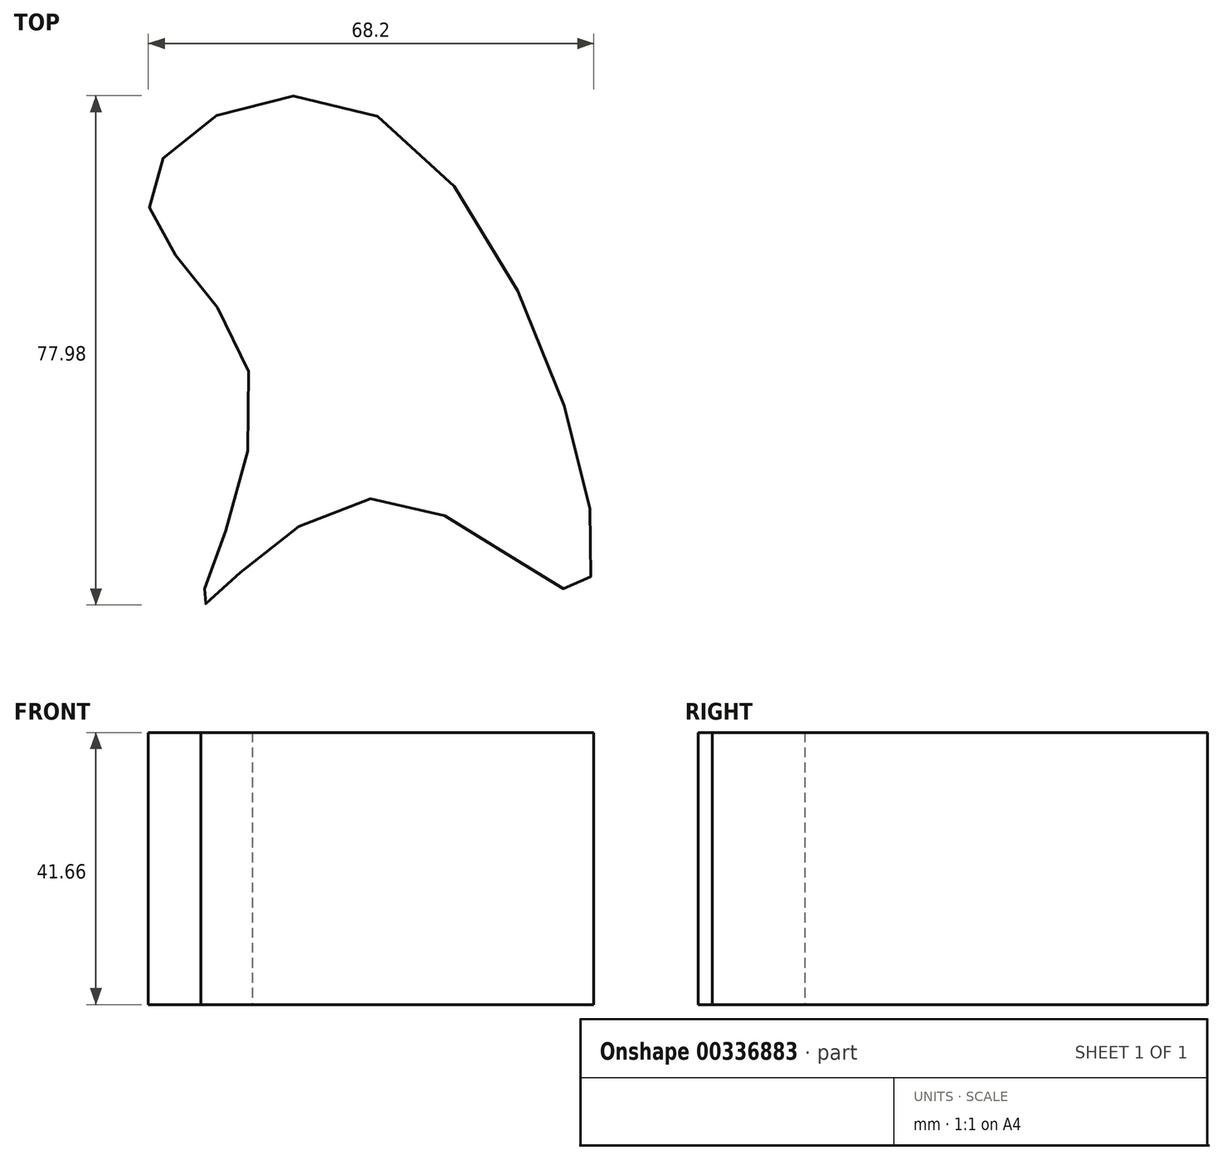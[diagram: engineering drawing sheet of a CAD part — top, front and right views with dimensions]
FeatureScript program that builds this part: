
annotation { "Feature Type Name" : "Feature", "Feature Type Description" : "" }
export const myFeature = defineFeature(function(context is Context, id is Id, definition is map)
    precondition{}
    {
        {
            var Q0;
            Q0=qCreatedBy(makeId("Top.planeOp"),FACE);
            var sketch = newSketch(context, id + "F0", { "sketchPlane" : qUnion([Q0])});
            skFitSpline(sketch, "E0", {"points": [v(0, 40.57) * mm, v(-35.01, 29.09) * mm, v(-19.45, 0) * mm, v(-26.86, -34.27) * mm, v(0, -17.97) * mm, v(31.68, -31.68) * mm, v(0, 40.57) * mm]});
            skSolve(sketch);
        }
        {
            var Q0;
            Q0=makeQuery(id+"F0.imprint","IMPRINT",FACE,{"disambiguationData":[TD([[makeQuery(id+"F0.imprint","IMPRINT",EDGE,{"derivedFrom":sQuery(id+"F0.wireOp",EDGE,"E0")}),1.0]])]});
            extrude(context, id + "F1", {"entities" : qUnion([Q0]), "depth" : 41.66 * mm});
        }
    });
